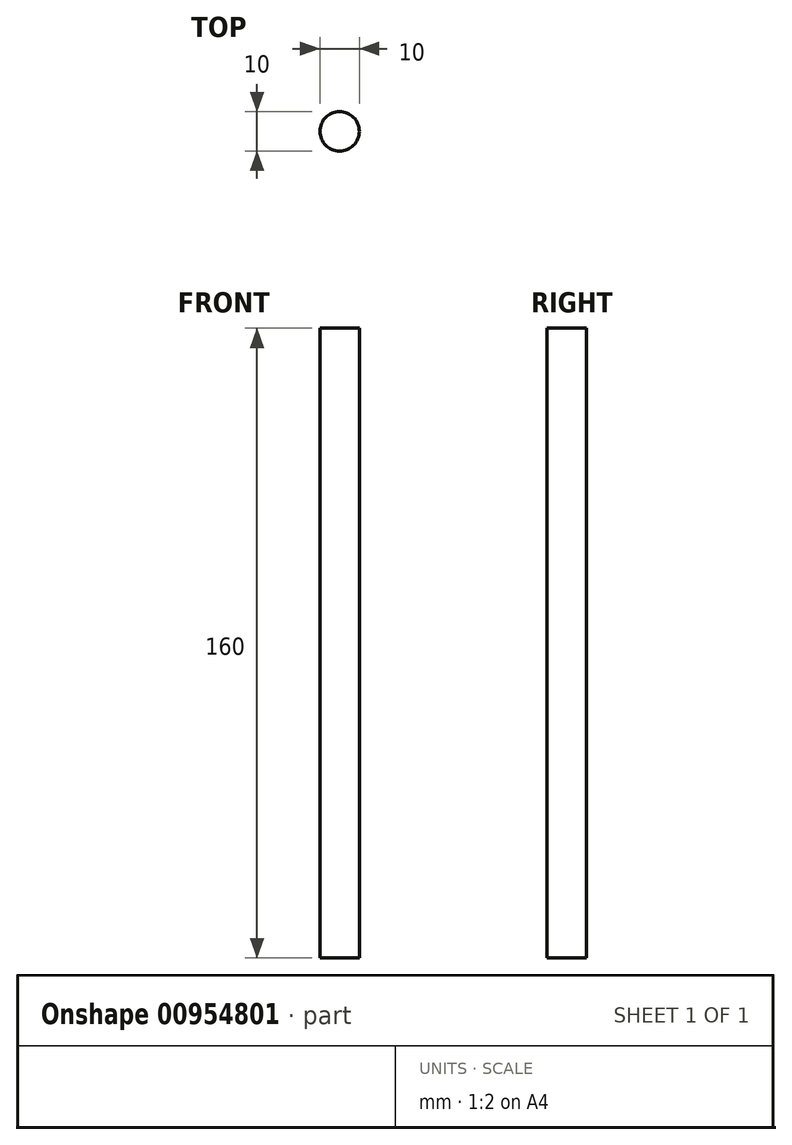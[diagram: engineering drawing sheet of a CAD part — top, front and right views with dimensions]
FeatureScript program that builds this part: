
annotation { "Feature Type Name" : "Feature", "Feature Type Description" : "" }
export const myFeature = defineFeature(function(context is Context, id is Id, definition is map)
    precondition{}
    {
        {
            var Q0;
            Q0=qCreatedBy(makeId("Top.planeOp"),FACE);
            var sketch = newSketch(context, id + "F0", { "sketchPlane" : qUnion([Q0])});
            skCircle(sketch, "E0", {"center": v(0, 0) * mm, "radius": 5 * mm});
            skSolve(sketch);
        }
        {
            var Q0;
            Q0=makeQuery(id+"F0.imprint","IMPRINT",FACE,{"disambiguationData":[TD([[makeQuery(id+"F0.imprint","IMPRINT",EDGE,{"derivedFrom":sQuery(id+"F0.wireOp",EDGE,"E0")}),1.0]])]});
            extrude(context, id + "F1", {"entities" : qUnion([Q0]), "depth" : 160 * mm, "offsetDistance" : 25 * mm});
        }
    });
